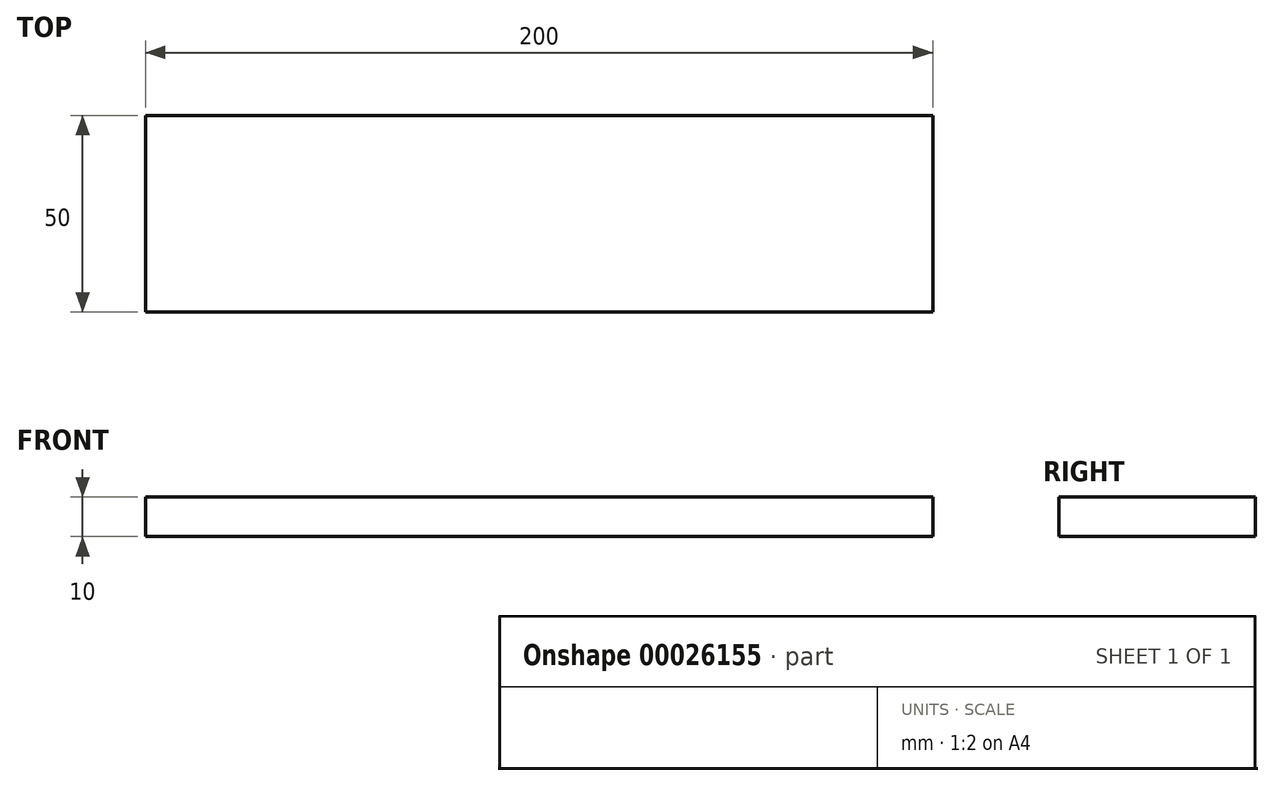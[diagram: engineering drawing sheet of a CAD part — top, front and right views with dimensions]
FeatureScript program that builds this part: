
annotation { "Feature Type Name" : "Feature", "Feature Type Description" : "" }
export const myFeature = defineFeature(function(context is Context, id is Id, definition is map)
    precondition{}
    {
        {
            var Q0;
            Q0=qCreatedBy(makeId("Top.planeOp"),FACE);
            var sketch = newSketch(context, id + "F0", { "sketchPlane" : qUnion([Q0])});
            skLineSegment(sketch, "E0.bottom", {"start": v(-49.61, 37.78) * mm, "end": v(150.39, 37.78) * mm});
            skLineSegment(sketch, "E0.top", {"start": v(-49.61, -12.22) * mm, "end": v(150.39, -12.22) * mm});
            skLineSegment(sketch, "E0.left", {"start": v(-49.61, 37.78) * mm, "end": v(-49.61, -12.22) * mm});
            skLineSegment(sketch, "E0.right", {"start": v(150.39, 37.78) * mm, "end": v(150.39, -12.22) * mm});
            skSolve(sketch);
        }
        {
            var Q0;
            Q0=makeQuery(id+"F0.imprint","IMPRINT",FACE,{"disambiguationData":[TD([[makeQuery(id+"F0.imprint","IMPRINT",EDGE,{"derivedFrom":sQuery(id+"F0.wireOp",EDGE,"E0.bottom")}),-1.0]])]});
            extrude(context, id + "F1", {"entities" : qUnion([Q0]), "depth" : 10 * mm});
        }
    });
